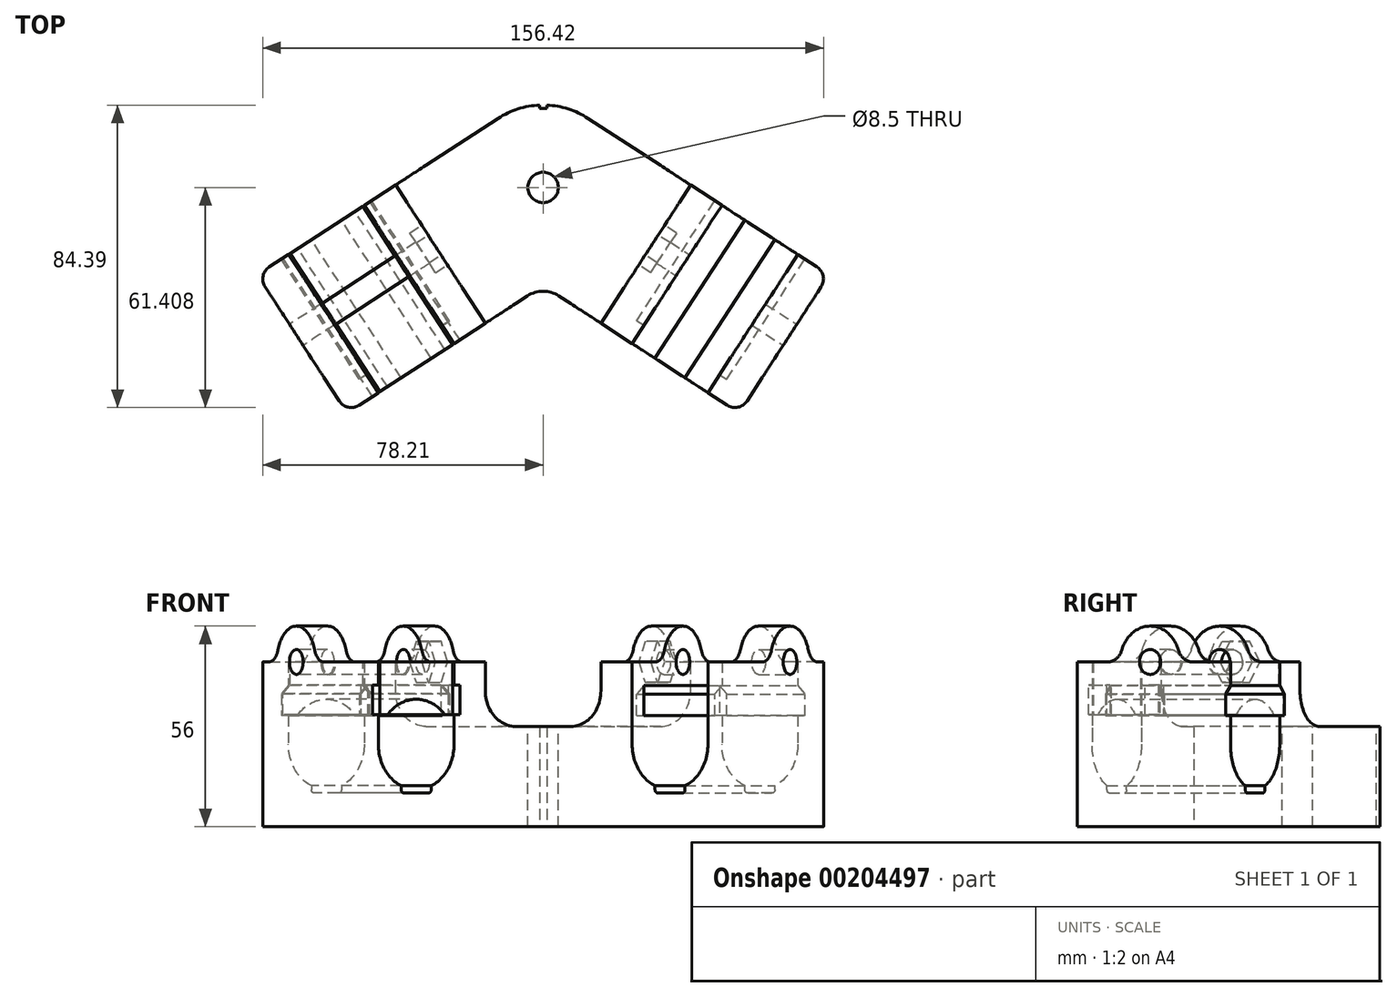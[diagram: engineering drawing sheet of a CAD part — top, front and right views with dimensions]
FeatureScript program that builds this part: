
annotation { "Feature Type Name" : "Feature", "Feature Type Description" : "" }
export const myFeature = defineFeature(function(context is Context, id is Id, definition is map)
    precondition{}
    {
        {
            var Q0;
            Q0=qCreatedBy(makeId("Top.planeOp"),FACE);
            var sketch = newSketch(context, id + "F0", { "sketchPlane" : qUnion([Q0])});
            skCircle(sketch, "E0", {"center": v(0, 0) * mm, "radius": 104.93 * mm, "construction": true});
            skLineSegment(sketch, "E1", {"start": v(0, 0) * mm, "end": v(-57.15, 88) * mm, "construction": true});
            skLineSegment(sketch, "E2", {"start": v(0, 0) * mm, "end": v(57.15, 88) * mm, "construction": true});
            skLineSegment(sketch, "E3", {"start": v(-54.7, 41.99) * mm, "end": v(0, 77.5) * mm});
            skLineSegment(sketch, "E4", {"start": v(-54.7, 41.99) * mm, "end": v(-79.74, 80.57) * mm});
            skLineSegment(sketch, "E5", {"start": v(-79.74, 80.57) * mm, "end": v(-12.53, 124.22) * mm});
            skArc(sketch, "E6", {"start": v(0, 127.93) * mm, "mid": v(-6.53, 126.98) * mm, "end": v(-12.53, 124.22) * mm});
            skLineSegment(sketch, "E7.MirrorCS", {"start": v(54.7, 41.99) * mm, "end": v(0, 77.5) * mm});
            skLineSegment(sketch, "E8.MirrorCS", {"start": v(79.74, 80.57) * mm, "end": v(12.53, 124.22) * mm});
            skLineSegment(sketch, "E9.MirrorCS", {"start": v(54.7, 41.99) * mm, "end": v(79.74, 80.57) * mm});
            skArc(sketch, "E10.MirrorCS", {"start": v(0, 127.93) * mm, "mid": v(6.53, 126.98) * mm, "end": v(12.53, 124.22) * mm});
            skPoint(sketch, "E11", {"position": v(-35.4, 54.51) * mm});
            skPoint(sketch, "E12", {"position": v(35.4, 54.51) * mm});
            skSolve(sketch);
        }
        {
            var Q0;
            Q0 = qSketchRegion(id + "F0", true);
            extrude(context, id + "F1", {"entities" : qUnion([Q0]), "endBound" : BoundingType.SYMMETRIC, "depth" : 46 * mm});
        }
        {
            var Q0;
            Q0=qCreatedBy(makeId("Top.planeOp"),FACE);
            var sketch = newSketch(context, id + "F2", { "sketchPlane" : qUnion([Q0])});
            skLineSegment(sketch, "E13", {"start": v(-45.97, 47.65) * mm, "end": v(-71.02, 86.23) * mm});
            skLineSegment(sketch, "E14", {"start": v(-71.02, 86.23) * mm, "end": v(-60.45, 93.1) * mm});
            skLineSegment(sketch, "E15", {"start": v(-60.45, 93.1) * mm, "end": v(-35.4, 54.51) * mm});
            skLineSegment(sketch, "E16", {"start": v(-35.4, 54.51) * mm, "end": v(-45.97, 47.65) * mm});
            skSolve(sketch);
        }
        {
            var Q0;
            Q0=qCreatedBy(makeId("Top.planeOp"),FACE);
            var sketch = newSketch(context, id + "F3", { "sketchPlane" : qUnion([Q0])});
            skLineSegment(sketch, "E17", {"start": v(24.83, 61.38) * mm, "end": v(49.89, 99.95) * mm});
            skLineSegment(sketch, "E18", {"start": v(49.89, 99.95) * mm, "end": v(60.45, 93.1) * mm});
            skLineSegment(sketch, "E19", {"start": v(60.45, 93.1) * mm, "end": v(35.4, 54.51) * mm});
            skLineSegment(sketch, "E20", {"start": v(35.4, 54.51) * mm, "end": v(24.83, 61.38) * mm});
            skSolve(sketch);
        }
        {
            var Q0;
            Q0 = qSketchRegion(id + "F2", true);
            var Q1;
            Q1=sQuery(id+"F0.wireOp",EDGE,"E1");
            revolve(context, id + "F4", {"operationType" : NewBodyOperationType.REMOVE, "entities" : qUnion([Q0]), "axis" : qUnion([Q1]), "revolveType" : RevolveType.FULL, "oppositeDirection" : true});
        }
        {
            var Q0;
            Q0 = qSketchRegion(id + "F3", true);
            var Q1;
            Q1=sQuery(id+"F0.wireOp",EDGE,"E2");
            revolve(context, id + "F5", {"operationType" : NewBodyOperationType.REMOVE, "entities" : qUnion([Q0]), "axis" : qUnion([Q1]), "revolveType" : RevolveType.FULL, "oppositeDirection" : true});
        }
        {
            var Q0;
            {var subQ0=sQuery(id+"F0.wireOp",EDGE,"E7.MirrorCS");var subQ1=makeQuery(id+"F1.opExtrude","SWEPT_FACE",FACE,{"disambiguationData":[OSD([subQ0])]});var subQ2=sQuery(id+"F0.wireOp",EDGE,"E10.MirrorCS");var subQ3=sQuery(id+"F0.wireOp",EDGE,"E6");var subQ5=sQuery(id+"F0.wireOp",EDGE,"E5");var subQ7=sQuery(id+"F0.wireOp",EDGE,"E3");var subQ8=makeQuery(id+"F1.opExtrude","SWEPT_FACE",FACE,{"disambiguationData":[OSD([subQ7])]});var subQ10=sQuery(id+"F0.wireOp",EDGE,"E8.MirrorCS");var subQ12=sQuery(id+"F0.wireOp",EDGE,"E9.MirrorCS");Q0=makeQuery(id+"F15.boolean.opBoolean","SPLIT",FACE,{"disambiguationData":[TD([subQ8])],"derivedFrom":makeQuery(id+"F14.boolean.opBoolean","SPLIT",FACE,{"disambiguationData":[TD([subQ1])],"derivedFrom":makeQuery(id+"F1.opExtrude","CAP_FACE",FACE,{"disambiguationData":[OSD([subQ7,sQuery(id+"F0.wireOp",EDGE,"E4"),subQ5,subQ3,subQ0,subQ10,subQ12,subQ2])],"isStart":false})})});}
            var sketch = newSketch(context, id + "F6", { "sketchPlane" : qUnion([Q0])});
            skLineSegment(sketch, "E21.0", {"start": v(-41.17, 105.62) * mm, "end": v(-12.53, 124.22) * mm});
            skArc(sketch, "E22.0", {"start": v(0, 127.93) * mm, "mid": v(-6.53, 126.98) * mm, "end": v(-12.53, 124.22) * mm});
            skArc(sketch, "E23.0", {"start": v(0, 127.93) * mm, "mid": v(6.53, 126.98) * mm, "end": v(12.53, 124.22) * mm});
            skLineSegment(sketch, "E24.0", {"start": v(41.17, 105.62) * mm, "end": v(12.53, 124.22) * mm});
            skLineSegment(sketch, "E25.0", {"start": v(16.11, 67.04) * mm, "end": v(0, 77.5) * mm});
            skLineSegment(sketch, "E26.0", {"start": v(-16.11, 67.04) * mm, "end": v(0, 77.5) * mm});
            skLineSegment(sketch, "E27", {"start": v(-41.17, 105.62) * mm, "end": v(-16.11, 67.04) * mm});
            skLineSegment(sketch, "E28", {"start": v(16.11, 67.04) * mm, "end": v(41.17, 105.62) * mm});
            skPoint(sketch, "E29.orphan", {"position": v(-79.74, 80.57) * mm});
            skPoint(sketch, "E30.orphan", {"position": v(-54.7, 41.99) * mm});
            skPoint(sketch, "E31.orphan", {"position": v(54.7, 41.99) * mm});
            skPoint(sketch, "E32.orphan", {"position": v(79.74, 80.57) * mm});
            skSolve(sketch);
        }
        {
            var Q0;
            Q0 = qSketchRegion(id + "F6", true);
            extrude(context, id + "F7", {"entities" : qUnion([Q0]), "operationType" : NewBodyOperationType.REMOVE, "oppositeDirection" : true, "depth" : 18 * mm});
        }
        {
            var Q0;
            Q0=makeQuery(id+"F1.opExtrude","SWEPT_FACE",FACE,{"disambiguationData":[OSD([sQuery(id+"F0.wireOp",EDGE,"E4")])]});
            var sketch = newSketch(context, id + "F8", { "sketchPlane" : qUnion([Q0])});
            skCircle(sketch, "E33", {"center": v(-91, 23) * mm, "radius": 10 * mm});
            skSolve(sketch);
        }
        {
            var Q0;
            Q0=makeQuery(id+"F1.opExtrude","SWEPT_FACE",FACE,{"disambiguationData":[OSD([sQuery(id+"F0.wireOp",EDGE,"E9.MirrorCS")])]});
            var sketch = newSketch(context, id + "F9", { "sketchPlane" : qUnion([Q0])});
            skCircle(sketch, "E34", {"center": v(91, 23) * mm, "radius": 10 * mm});
            skSolve(sketch);
        }
        {
            var Q0;
            Q0 = qSketchRegion(id + "F8", true);
            var Q1;
            Q1=makeQuery(id+"F7.boolean.opBoolean","COPY",FACE,{"derivedFrom":makeQuery(id+"F7.opExtrude","SWEPT_FACE",FACE,{"disambiguationData":[OSD([sQuery(id+"F6.wireOp",EDGE,"E27")])]})});
            extrude(context, id + "F10", {"entities" : qUnion([Q0]), "operationType" : NewBodyOperationType.ADD, "endBound" : BoundingType.UP_TO_SURFACE, "oppositeDirection" : true, "endBoundEntityFace" : qUnion([Q1]), "depth" : 25 * mm});
        }
        {
            var Q0;
            Q0 = qSketchRegion(id + "F9", true);
            var Q1;
            Q1=makeQuery(id+"F7.boolean.opBoolean","COPY",FACE,{"derivedFrom":makeQuery(id+"F7.opExtrude","SWEPT_FACE",FACE,{"disambiguationData":[OSD([sQuery(id+"F6.wireOp",EDGE,"E28")])]})});
            extrude(context, id + "F11", {"entities" : qUnion([Q0]), "operationType" : NewBodyOperationType.ADD, "endBound" : BoundingType.UP_TO_SURFACE, "oppositeDirection" : true, "endBoundEntityFace" : qUnion([Q1]), "depth" : 25 * mm});
        }
        {
            var Q0;
            Q0=qCreatedBy(makeId("Top.planeOp"),FACE);
            var sketch = newSketch(context, id + "F12", { "sketchPlane" : qUnion([Q0])});
            skLineSegment(sketch, "E35.0", {"start": v(-45.97, 47.65) * mm, "end": v(-71.02, 86.23) * mm});
            skLineSegment(sketch, "E36.0", {"start": v(-35.4, 54.51) * mm, "end": v(-45.97, 47.65) * mm});
            skLineSegment(sketch, "E37.0", {"start": v(-71.02, 86.23) * mm, "end": v(-60.45, 93.1) * mm});
            skLineSegment(sketch, "E38.MirrorCS", {"start": v(-35.4, 54.51) * mm, "end": v(-24.83, 61.38) * mm});
            skLineSegment(sketch, "E39.MirrorCS", {"start": v(-24.83, 61.38) * mm, "end": v(-49.89, 99.95) * mm});
            skLineSegment(sketch, "E40.MirrorCS", {"start": v(-49.89, 99.95) * mm, "end": v(-60.45, 93.1) * mm});
            skSolve(sketch);
        }
        {
            var Q0;
            Q0=qCreatedBy(makeId("Top.planeOp"),FACE);
            var sketch = newSketch(context, id + "F13", { "sketchPlane" : qUnion([Q0])});
            skLineSegment(sketch, "E41.0", {"start": v(35.4, 54.51) * mm, "end": v(24.83, 61.38) * mm});
            skLineSegment(sketch, "E42.0", {"start": v(24.83, 61.38) * mm, "end": v(49.89, 99.95) * mm});
            skLineSegment(sketch, "E43.0", {"start": v(49.89, 99.95) * mm, "end": v(60.45, 93.1) * mm});
            skLineSegment(sketch, "E44.MirrorCS", {"start": v(45.97, 47.65) * mm, "end": v(71.02, 86.23) * mm});
            skLineSegment(sketch, "E45.MirrorCS", {"start": v(35.4, 54.51) * mm, "end": v(45.97, 47.65) * mm});
            skLineSegment(sketch, "E46.MirrorCS", {"start": v(71.02, 86.23) * mm, "end": v(60.45, 93.1) * mm});
            skSolve(sketch);
        }
        {
            var Q0;
            Q0 = qSketchRegion(id + "F12", true);
            var Q1;
            Q1=makeQuery(id+"F1.opExtrude","CAP_FACE",FACE,{"disambiguationData":[OSD([sQuery(id+"F0.wireOp",EDGE,"E3"),sQuery(id+"F0.wireOp",EDGE,"E4"),sQuery(id+"F0.wireOp",EDGE,"E5"),sQuery(id+"F0.wireOp",EDGE,"E6"),sQuery(id+"F0.wireOp",EDGE,"E7.MirrorCS"),sQuery(id+"F0.wireOp",EDGE,"E8.MirrorCS"),sQuery(id+"F0.wireOp",EDGE,"E9.MirrorCS"),sQuery(id+"F0.wireOp",EDGE,"E10.MirrorCS")])],"isStart":false});
            extrude(context, id + "F14", {"entities" : qUnion([Q0]), "operationType" : NewBodyOperationType.REMOVE, "endBound" : BoundingType.THROUGH_ALL, "endBoundEntityFace" : qUnion([Q1]), "depth" : 25 * mm});
        }
        {
            var Q0;
            Q0 = qSketchRegion(id + "F13", true);
            var Q1;
            {var subQ0=sQuery(id+"F0.wireOp",EDGE,"E7.MirrorCS");var subQ1=sQuery(id+"F0.wireOp",EDGE,"E8.MirrorCS");var subQ2=sQuery(id+"F0.wireOp",EDGE,"E9.MirrorCS");Q1=makeQuery(id+"F7.boolean.opBoolean","SPLIT",FACE,{"disambiguationData":[TD([makeQuery(id+"F1.opExtrude","SWEPT_FACE",FACE,{"disambiguationData":[OSD([subQ0])]})])],"derivedFrom":makeQuery(id+"F1.opExtrude","CAP_FACE",FACE,{"disambiguationData":[OSD([sQuery(id+"F0.wireOp",EDGE,"E3"),sQuery(id+"F0.wireOp",EDGE,"E4"),sQuery(id+"F0.wireOp",EDGE,"E5"),sQuery(id+"F0.wireOp",EDGE,"E6"),subQ0,subQ1,subQ2,sQuery(id+"F0.wireOp",EDGE,"E10.MirrorCS")])],"isStart":false})});}
            extrude(context, id + "F15", {"entities" : qUnion([Q0]), "operationType" : NewBodyOperationType.REMOVE, "endBound" : BoundingType.THROUGH_ALL, "endBoundEntityFace" : qUnion([Q1]), "depth" : 25 * mm});
        }
        {
            var Q0;
            Q0=makeQuery(id+"F1.opExtrude","SWEPT_EDGE",EDGE,{"disambiguationData":[OSD([sQuery(id+"F0.wireOp",EDGE,"E3"),sQuery(id+"F0.wireOp",EDGE,"E7.MirrorCS")])]});
            fillet(context, id + "F16", {"entities" : qUnion([Q0]), "radius" : 8 * mm, "tangentPropagation" : true, "allowEdgeOverflow" : false});
        }
        {
            var Q0;
            Q0=makeQuery(id+"F7.boolean.opBoolean","COPY",EDGE,{"derivedFrom":makeQuery(id+"F7.opExtrude","CAP_EDGE",EDGE,{"disambiguationData":[OSD([sQuery(id+"F6.wireOp",EDGE,"E28")])],"isStart":false})});
            var Q1;
            Q1=makeQuery(id+"F7.boolean.opBoolean","COPY",EDGE,{"derivedFrom":makeQuery(id+"F7.opExtrude","CAP_EDGE",EDGE,{"disambiguationData":[OSD([sQuery(id+"F6.wireOp",EDGE,"E27")])],"isStart":false})});
            fillet(context, id + "F17", {"entities" : qUnion([Q0, Q1]), "radius" : 10 * mm, "tangentPropagation" : true, "allowEdgeOverflow" : false});
        }
        {
            var Q0;
            Q0=makeQuery(id+"F1.opExtrude","SWEPT_FACE",FACE,{"disambiguationData":[OSD([sQuery(id+"F0.wireOp",EDGE,"E5")])]});
            var sketch = newSketch(context, id + "F18", { "sketchPlane" : qUnion([Q0])});
            skLineSegment(sketch, "E47.bottom", {"start": v(-12.6, 16.4) * mm, "end": v(12.6, 16.4) * mm});
            skLineSegment(sketch, "E47.top", {"start": v(-15, 8) * mm, "end": v(15, 8) * mm});
            skLineSegment(sketch, "E47.left", {"start": v(-15, 14) * mm, "end": v(-15, 8) * mm});
            skLineSegment(sketch, "E47.right", {"start": v(15, 14) * mm, "end": v(15, 8) * mm});
            skLineSegment(sketch, "E48", {"start": v(-12.6, 16.4) * mm, "end": v(-15, 14) * mm});
            skLineSegment(sketch, "E49", {"start": v(12.6, 16.4) * mm, "end": v(15, 14) * mm});
            skSolve(sketch);
        }
        {
            var Q0;
            Q0=makeQuery(id+"F1.opExtrude","SWEPT_FACE",FACE,{"disambiguationData":[OSD([sQuery(id+"F0.wireOp",EDGE,"E8.MirrorCS")])]});
            var sketch = newSketch(context, id + "F19", { "sketchPlane" : qUnion([Q0])});
            skLineSegment(sketch, "E50.bottom", {"start": v(-15, 8) * mm, "end": v(15, 8) * mm});
            skLineSegment(sketch, "E50.top", {"start": v(-12.6, 16.4) * mm, "end": v(12.6, 16.4) * mm});
            skLineSegment(sketch, "E50.left", {"start": v(-15, 8) * mm, "end": v(-15, 14) * mm});
            skLineSegment(sketch, "E50.right", {"start": v(15, 8) * mm, "end": v(15, 14) * mm});
            skLineSegment(sketch, "E51", {"start": v(-12.6, 16.4) * mm, "end": v(-15, 14) * mm});
            skLineSegment(sketch, "E52", {"start": v(12.6, 16.4) * mm, "end": v(15, 14) * mm});
            skSolve(sketch);
        }
        {
            var Q0;
            Q0 = qSketchRegion(id + "F18", true);
            extrude(context, id + "F20", {"entities" : qUnion([Q0]), "operationType" : NewBodyOperationType.REMOVE, "oppositeDirection" : true, "depth" : 40 * mm});
        }
        {
            var Q0;
            Q0 = qSketchRegion(id + "F19", true);
            extrude(context, id + "F21", {"entities" : qUnion([Q0]), "operationType" : NewBodyOperationType.REMOVE, "oppositeDirection" : true, "depth" : 40 * mm});
        }
        {
            var Q0;
            Q0=makeQuery(id+"F1.opExtrude","SWEPT_FACE",FACE,{"disambiguationData":[OSD([sQuery(id+"F0.wireOp",EDGE,"E5")])]});
            var sketch = newSketch(context, id + "F22", { "sketchPlane" : qUnion([Q0])});
            skLineSegment(sketch, "E53.bottom", {"start": v(-5, -10.6) * mm, "end": v(5, -10.6) * mm});
            skLineSegment(sketch, "E53.top", {"start": v(-4, -13.6) * mm, "end": v(4, -13.6) * mm});
            skLineSegment(sketch, "E53.left", {"start": v(-5, -10.6) * mm, "end": v(-5, -12.6) * mm});
            skLineSegment(sketch, "E53.right", {"start": v(5, -10.6) * mm, "end": v(5, -12.6) * mm});
            skLineSegment(sketch, "E54", {"start": v(0, 0) * mm, "end": v(0, -16.56) * mm, "construction": true});
            skPoint(sketch, "E54.endSnap0", {"position": v(0, -12.6) * mm});
            skPoint(sketch, "E55", {"position": v(0, -13.6) * mm});
            skPoint(sketch, "E56.visualSharp", {"position": v(-5, -13.6) * mm});
            skArc(sketch, "E56.filletArc", {"start": v(-5, -12.6) * mm, "mid": v(-4.7, -13.3) * mm, "end": v(-4, -13.6) * mm});
            skPoint(sketch, "E57.visualSharp", {"position": v(5, -13.6) * mm});
            skArc(sketch, "E57.filletArc", {"start": v(4, -13.6) * mm, "mid": v(4.7, -13.3) * mm, "end": v(5, -12.6) * mm});
            skSolve(sketch);
        }
        {
            var Q0;
            Q0=makeQuery(id+"F1.opExtrude","SWEPT_FACE",FACE,{"disambiguationData":[OSD([sQuery(id+"F0.wireOp",EDGE,"E8.MirrorCS")])]});
            var sketch = newSketch(context, id + "F23", { "sketchPlane" : qUnion([Q0])});
            skLineSegment(sketch, "E58.bottom", {"start": v(-4, -13.6) * mm, "end": v(4, -13.6) * mm});
            skLineSegment(sketch, "E58.top", {"start": v(-5, -10.6) * mm, "end": v(5, -10.6) * mm});
            skLineSegment(sketch, "E58.left", {"start": v(-5, -12.6) * mm, "end": v(-5, -10.6) * mm});
            skLineSegment(sketch, "E58.right", {"start": v(5, -12.6) * mm, "end": v(5, -10.6) * mm});
            skLineSegment(sketch, "E59", {"start": v(0, 0) * mm, "end": v(0, -15.9) * mm, "construction": true});
            skPoint(sketch, "E59.endSnap0", {"position": v(0, -12.6) * mm});
            skPoint(sketch, "E60", {"position": v(0, -13.6) * mm});
            skPoint(sketch, "E61.visualSharp", {"position": v(-5, -13.6) * mm});
            skArc(sketch, "E61.filletArc", {"start": v(-5, -12.6) * mm, "mid": v(-4.7, -13.3) * mm, "end": v(-4, -13.6) * mm});
            skPoint(sketch, "E62.visualSharp", {"position": v(5, -13.6) * mm});
            skArc(sketch, "E62.filletArc", {"start": v(4, -13.6) * mm, "mid": v(4.7, -13.3) * mm, "end": v(5, -12.6) * mm});
            skSolve(sketch);
        }
        {
            var Q0;
            Q0 = qSketchRegion(id + "F22", true);
            var Q1;
            Q1=makeQuery(id+"F1.opExtrude","SWEPT_FACE",FACE,{"disambiguationData":[OSD([sQuery(id+"F0.wireOp",EDGE,"E3")])]});
            extrude(context, id + "F24", {"entities" : qUnion([Q0]), "operationType" : NewBodyOperationType.REMOVE, "endBound" : BoundingType.UP_TO_SURFACE, "oppositeDirection" : true, "endBoundEntityFace" : qUnion([Q1]), "depth" : 25 * mm});
        }
        {
            var Q0;
            Q0 = qSketchRegion(id + "F23", true);
            var Q1;
            Q1=makeQuery(id+"F1.opExtrude","SWEPT_FACE",FACE,{"disambiguationData":[OSD([sQuery(id+"F0.wireOp",EDGE,"E7.MirrorCS")])]});
            extrude(context, id + "F25", {"entities" : qUnion([Q0]), "operationType" : NewBodyOperationType.REMOVE, "endBound" : BoundingType.UP_TO_SURFACE, "oppositeDirection" : true, "endBoundEntityFace" : qUnion([Q1]), "depth" : 25 * mm});
        }
        {
            var Q0;
            {var subQ0=sQuery(id+"F9.wireOp",EDGE,"E34");var subQ1=makeQuery(id+"F11.opExtrude","SWEPT_FACE",FACE,{"disambiguationData":[OSD([subQ0])]});var subQ2=sQuery(id+"F0.wireOp",EDGE,"E9.MirrorCS");var subQ3=makeQuery(id+"F1.opExtrude","SWEPT_FACE",FACE,{"disambiguationData":[OSD([subQ2])]});var subQ4=sQuery(id+"F0.wireOp",EDGE,"E8.MirrorCS");var subQ5=sQuery(id+"F0.wireOp",EDGE,"E7.MirrorCS");var subQ6=makeQuery(id+"F1.opExtrude","CAP_FACE",FACE,{"disambiguationData":[OSD([sQuery(id+"F0.wireOp",EDGE,"E3"),sQuery(id+"F0.wireOp",EDGE,"E4"),sQuery(id+"F0.wireOp",EDGE,"E5"),sQuery(id+"F0.wireOp",EDGE,"E6"),subQ5,subQ4,subQ2,sQuery(id+"F0.wireOp",EDGE,"E10.MirrorCS")])],"isStart":false});Q0=makeQuery(id+"F15.boolean.opBoolean","SPLIT",EDGE,{"disambiguationData":[TD([subQ3])],"derivedFrom":makeQuery(id+"F11.boolean.opBoolean","INTERSECT",EDGE,{"disambiguationData":[OD(1.0)],"derivedFrom":[makeQuery(id+"F7.boolean.opBoolean","SPLIT",FACE,{"disambiguationData":[TD([makeQuery(id+"F1.opExtrude","SWEPT_FACE",FACE,{"disambiguationData":[OSD([subQ5])]})])],"derivedFrom":subQ6}),subQ1]})});}
            var Q1;
            {var subQ0=sQuery(id+"F9.wireOp",EDGE,"E34");var subQ1=makeQuery(id+"F11.opExtrude","SWEPT_FACE",FACE,{"disambiguationData":[OSD([subQ0])]});var subQ2=sQuery(id+"F0.wireOp",EDGE,"E9.MirrorCS");var subQ3=makeQuery(id+"F1.opExtrude","SWEPT_FACE",FACE,{"disambiguationData":[OSD([subQ2])]});var subQ4=sQuery(id+"F0.wireOp",EDGE,"E8.MirrorCS");var subQ5=sQuery(id+"F0.wireOp",EDGE,"E7.MirrorCS");var subQ6=makeQuery(id+"F1.opExtrude","CAP_FACE",FACE,{"disambiguationData":[OSD([sQuery(id+"F0.wireOp",EDGE,"E3"),sQuery(id+"F0.wireOp",EDGE,"E4"),sQuery(id+"F0.wireOp",EDGE,"E5"),sQuery(id+"F0.wireOp",EDGE,"E6"),subQ5,subQ4,subQ2,sQuery(id+"F0.wireOp",EDGE,"E10.MirrorCS")])],"isStart":false});Q1=makeQuery(id+"F15.boolean.opBoolean","SPLIT",EDGE,{"disambiguationData":[TD([subQ3])],"derivedFrom":makeQuery(id+"F11.boolean.opBoolean","INTERSECT",EDGE,{"disambiguationData":[OD(0.0)],"derivedFrom":[makeQuery(id+"F7.boolean.opBoolean","SPLIT",FACE,{"disambiguationData":[TD([makeQuery(id+"F1.opExtrude","SWEPT_FACE",FACE,{"disambiguationData":[OSD([subQ5])]})])],"derivedFrom":subQ6}),subQ1]})});}
            var Q2;
            {var subQ0=makeQuery(id+"F11.opExtrude","SWEPT_FACE",FACE,{"disambiguationData":[OSD([sQuery(id+"F9.wireOp",EDGE,"E34")])]});var subQ1=sQuery(id+"F6.wireOp",EDGE,"E28");var subQ2=makeQuery(id+"F7.opExtrude","SWEPT_FACE",FACE,{"disambiguationData":[OSD([subQ1])]});var subQ3=sQuery(id+"F0.wireOp",EDGE,"E9.MirrorCS");var subQ4=sQuery(id+"F0.wireOp",EDGE,"E8.MirrorCS");var subQ5=sQuery(id+"F0.wireOp",EDGE,"E7.MirrorCS");var subQ6=makeQuery(id+"F1.opExtrude","CAP_FACE",FACE,{"disambiguationData":[OSD([sQuery(id+"F0.wireOp",EDGE,"E3"),sQuery(id+"F0.wireOp",EDGE,"E4"),sQuery(id+"F0.wireOp",EDGE,"E5"),sQuery(id+"F0.wireOp",EDGE,"E6"),subQ5,subQ4,subQ3,sQuery(id+"F0.wireOp",EDGE,"E10.MirrorCS")])],"isStart":false});Q2=makeQuery(id+"F15.boolean.opBoolean","SPLIT",EDGE,{"disambiguationData":[TD([makeQuery(id+"F7.boolean.opBoolean","COPY",FACE,{"derivedFrom":subQ2})])],"derivedFrom":makeQuery(id+"F11.boolean.opBoolean","INTERSECT",EDGE,{"disambiguationData":[OD(0.0)],"derivedFrom":[makeQuery(id+"F7.boolean.opBoolean","SPLIT",FACE,{"disambiguationData":[TD([makeQuery(id+"F1.opExtrude","SWEPT_FACE",FACE,{"disambiguationData":[OSD([subQ5])]})])],"derivedFrom":subQ6}),subQ0]})});}
            var Q3;
            {var subQ0=makeQuery(id+"F11.opExtrude","SWEPT_FACE",FACE,{"disambiguationData":[OSD([sQuery(id+"F9.wireOp",EDGE,"E34")])]});var subQ1=sQuery(id+"F6.wireOp",EDGE,"E28");var subQ2=makeQuery(id+"F7.opExtrude","SWEPT_FACE",FACE,{"disambiguationData":[OSD([subQ1])]});var subQ3=sQuery(id+"F0.wireOp",EDGE,"E9.MirrorCS");var subQ4=sQuery(id+"F0.wireOp",EDGE,"E8.MirrorCS");var subQ5=sQuery(id+"F0.wireOp",EDGE,"E7.MirrorCS");var subQ6=makeQuery(id+"F1.opExtrude","CAP_FACE",FACE,{"disambiguationData":[OSD([sQuery(id+"F0.wireOp",EDGE,"E3"),sQuery(id+"F0.wireOp",EDGE,"E4"),sQuery(id+"F0.wireOp",EDGE,"E5"),sQuery(id+"F0.wireOp",EDGE,"E6"),subQ5,subQ4,subQ3,sQuery(id+"F0.wireOp",EDGE,"E10.MirrorCS")])],"isStart":false});Q3=makeQuery(id+"F15.boolean.opBoolean","SPLIT",EDGE,{"disambiguationData":[TD([makeQuery(id+"F7.boolean.opBoolean","COPY",FACE,{"derivedFrom":subQ2})])],"derivedFrom":makeQuery(id+"F11.boolean.opBoolean","INTERSECT",EDGE,{"disambiguationData":[OD(1.0)],"derivedFrom":[makeQuery(id+"F7.boolean.opBoolean","SPLIT",FACE,{"disambiguationData":[TD([makeQuery(id+"F1.opExtrude","SWEPT_FACE",FACE,{"disambiguationData":[OSD([subQ5])]})])],"derivedFrom":subQ6}),subQ0]})});}
            var Q4;
            {var subQ0=makeQuery(id+"F10.opExtrude","SWEPT_FACE",FACE,{"disambiguationData":[OSD([sQuery(id+"F8.wireOp",EDGE,"E33")])]});var subQ1=sQuery(id+"F6.wireOp",EDGE,"E27");var subQ2=makeQuery(id+"F7.opExtrude","SWEPT_FACE",FACE,{"disambiguationData":[OSD([subQ1])]});var subQ3=sQuery(id+"F0.wireOp",EDGE,"E5");var subQ4=sQuery(id+"F0.wireOp",EDGE,"E4");var subQ5=sQuery(id+"F0.wireOp",EDGE,"E3");var subQ6=makeQuery(id+"F1.opExtrude","CAP_FACE",FACE,{"disambiguationData":[OSD([subQ5,subQ4,subQ3,sQuery(id+"F0.wireOp",EDGE,"E6"),sQuery(id+"F0.wireOp",EDGE,"E7.MirrorCS"),sQuery(id+"F0.wireOp",EDGE,"E8.MirrorCS"),sQuery(id+"F0.wireOp",EDGE,"E9.MirrorCS"),sQuery(id+"F0.wireOp",EDGE,"E10.MirrorCS")])],"isStart":false});Q4=makeQuery(id+"F14.boolean.opBoolean","SPLIT",EDGE,{"disambiguationData":[TD([makeQuery(id+"F7.boolean.opBoolean","COPY",FACE,{"derivedFrom":subQ2})])],"derivedFrom":makeQuery(id+"F10.boolean.opBoolean","INTERSECT",EDGE,{"disambiguationData":[OD(1.0)],"derivedFrom":[makeQuery(id+"F7.boolean.opBoolean","SPLIT",FACE,{"disambiguationData":[TD([makeQuery(id+"F1.opExtrude","SWEPT_FACE",FACE,{"disambiguationData":[OSD([subQ5])]})])],"derivedFrom":subQ6}),subQ0]})});}
            var Q5;
            {var subQ0=makeQuery(id+"F10.opExtrude","SWEPT_FACE",FACE,{"disambiguationData":[OSD([sQuery(id+"F8.wireOp",EDGE,"E33")])]});var subQ1=sQuery(id+"F6.wireOp",EDGE,"E27");var subQ2=makeQuery(id+"F7.opExtrude","SWEPT_FACE",FACE,{"disambiguationData":[OSD([subQ1])]});var subQ3=sQuery(id+"F0.wireOp",EDGE,"E5");var subQ4=sQuery(id+"F0.wireOp",EDGE,"E4");var subQ5=sQuery(id+"F0.wireOp",EDGE,"E3");var subQ6=makeQuery(id+"F1.opExtrude","CAP_FACE",FACE,{"disambiguationData":[OSD([subQ5,subQ4,subQ3,sQuery(id+"F0.wireOp",EDGE,"E6"),sQuery(id+"F0.wireOp",EDGE,"E7.MirrorCS"),sQuery(id+"F0.wireOp",EDGE,"E8.MirrorCS"),sQuery(id+"F0.wireOp",EDGE,"E9.MirrorCS"),sQuery(id+"F0.wireOp",EDGE,"E10.MirrorCS")])],"isStart":false});Q5=makeQuery(id+"F14.boolean.opBoolean","SPLIT",EDGE,{"disambiguationData":[TD([makeQuery(id+"F7.boolean.opBoolean","COPY",FACE,{"derivedFrom":subQ2})])],"derivedFrom":makeQuery(id+"F10.boolean.opBoolean","INTERSECT",EDGE,{"disambiguationData":[OD(0.0)],"derivedFrom":[makeQuery(id+"F7.boolean.opBoolean","SPLIT",FACE,{"disambiguationData":[TD([makeQuery(id+"F1.opExtrude","SWEPT_FACE",FACE,{"disambiguationData":[OSD([subQ5])]})])],"derivedFrom":subQ6}),subQ0]})});}
            var Q6;
            {var subQ0=sQuery(id+"F8.wireOp",EDGE,"E33");var subQ1=makeQuery(id+"F10.opExtrude","SWEPT_FACE",FACE,{"disambiguationData":[OSD([subQ0])]});var subQ2=sQuery(id+"F0.wireOp",EDGE,"E4");var subQ3=makeQuery(id+"F1.opExtrude","SWEPT_FACE",FACE,{"disambiguationData":[OSD([subQ2])]});var subQ4=sQuery(id+"F0.wireOp",EDGE,"E5");var subQ5=sQuery(id+"F0.wireOp",EDGE,"E3");var subQ6=makeQuery(id+"F1.opExtrude","CAP_FACE",FACE,{"disambiguationData":[OSD([subQ5,subQ2,subQ4,sQuery(id+"F0.wireOp",EDGE,"E6"),sQuery(id+"F0.wireOp",EDGE,"E7.MirrorCS"),sQuery(id+"F0.wireOp",EDGE,"E8.MirrorCS"),sQuery(id+"F0.wireOp",EDGE,"E9.MirrorCS"),sQuery(id+"F0.wireOp",EDGE,"E10.MirrorCS")])],"isStart":false});Q6=makeQuery(id+"F14.boolean.opBoolean","SPLIT",EDGE,{"disambiguationData":[TD([subQ3])],"derivedFrom":makeQuery(id+"F10.boolean.opBoolean","INTERSECT",EDGE,{"disambiguationData":[OD(0.0)],"derivedFrom":[makeQuery(id+"F7.boolean.opBoolean","SPLIT",FACE,{"disambiguationData":[TD([makeQuery(id+"F1.opExtrude","SWEPT_FACE",FACE,{"disambiguationData":[OSD([subQ5])]})])],"derivedFrom":subQ6}),subQ1]})});}
            var Q7;
            {var subQ0=sQuery(id+"F8.wireOp",EDGE,"E33");var subQ1=makeQuery(id+"F10.opExtrude","SWEPT_FACE",FACE,{"disambiguationData":[OSD([subQ0])]});var subQ2=sQuery(id+"F0.wireOp",EDGE,"E4");var subQ3=makeQuery(id+"F1.opExtrude","SWEPT_FACE",FACE,{"disambiguationData":[OSD([subQ2])]});var subQ4=sQuery(id+"F0.wireOp",EDGE,"E5");var subQ5=sQuery(id+"F0.wireOp",EDGE,"E3");var subQ6=makeQuery(id+"F1.opExtrude","CAP_FACE",FACE,{"disambiguationData":[OSD([subQ5,subQ2,subQ4,sQuery(id+"F0.wireOp",EDGE,"E6"),sQuery(id+"F0.wireOp",EDGE,"E7.MirrorCS"),sQuery(id+"F0.wireOp",EDGE,"E8.MirrorCS"),sQuery(id+"F0.wireOp",EDGE,"E9.MirrorCS"),sQuery(id+"F0.wireOp",EDGE,"E10.MirrorCS")])],"isStart":false});Q7=makeQuery(id+"F14.boolean.opBoolean","SPLIT",EDGE,{"disambiguationData":[TD([subQ3])],"derivedFrom":makeQuery(id+"F10.boolean.opBoolean","INTERSECT",EDGE,{"disambiguationData":[OD(1.0)],"derivedFrom":[makeQuery(id+"F7.boolean.opBoolean","SPLIT",FACE,{"disambiguationData":[TD([makeQuery(id+"F1.opExtrude","SWEPT_FACE",FACE,{"disambiguationData":[OSD([subQ5])]})])],"derivedFrom":subQ6}),subQ1]})});}
            fillet(context, id + "F26", {"entities" : qUnion([Q0, Q1, Q2, Q3, Q4, Q5, Q6, Q7]), "radius" : 5 * mm, "tangentPropagation" : true, "allowEdgeOverflow" : false});
        }
        {
            var Q0;
            Q0=makeQuery(id+"F7.boolean.opBoolean","COPY",FACE,{"derivedFrom":makeQuery(id+"F7.opExtrude","CAP_FACE",FACE,{"disambiguationData":[OSD([sQuery(id+"F6.wireOp",EDGE,"E21.0"),sQuery(id+"F6.wireOp",EDGE,"E22.0"),sQuery(id+"F6.wireOp",EDGE,"E23.0"),sQuery(id+"F6.wireOp",EDGE,"E24.0"),sQuery(id+"F6.wireOp",EDGE,"E25.0"),sQuery(id+"F6.wireOp",EDGE,"E26.0"),sQuery(id+"F6.wireOp",EDGE,"E27"),sQuery(id+"F6.wireOp",EDGE,"E28")])],"isStart":false})});
            var sketch = newSketch(context, id + "F27", { "sketchPlane" : qUnion([Q0])});
            skCircle(sketch, "E63", {"center": v(0, 104.93) * mm, "radius": 4.25 * mm});
            skLineSegment(sketch, "E64", {"start": v(0, 104.93) * mm, "end": v(0, 128.64) * mm, "construction": true});
            skLineSegment(sketch, "E65.bottom", {"start": v(1, 126.93) * mm, "end": v(-1, 126.93) * mm});
            skLineSegment(sketch, "E65.top", {"start": v(1, 128.93) * mm, "end": v(-1, 128.93) * mm});
            skLineSegment(sketch, "E65.left", {"start": v(1, 126.93) * mm, "end": v(1, 128.93) * mm});
            skLineSegment(sketch, "E65.right", {"start": v(-1, 126.93) * mm, "end": v(-1, 128.93) * mm});
            skPoint(sketch, "E66", {"position": v(0, 128.93) * mm});
            skSolve(sketch);
        }
        {
            var Q0;
            Q0 = qSketchRegion(id + "F27", true);
            var Q1;
            Q1=makeQuery(id+"F1.opExtrude","CAP_FACE",FACE,{"disambiguationData":[OSD([sQuery(id+"F0.wireOp",EDGE,"E3"),sQuery(id+"F0.wireOp",EDGE,"E4"),sQuery(id+"F0.wireOp",EDGE,"E5"),sQuery(id+"F0.wireOp",EDGE,"E6"),sQuery(id+"F0.wireOp",EDGE,"E7.MirrorCS"),sQuery(id+"F0.wireOp",EDGE,"E8.MirrorCS"),sQuery(id+"F0.wireOp",EDGE,"E9.MirrorCS"),sQuery(id+"F0.wireOp",EDGE,"E10.MirrorCS")])],"isStart":true});
            extrude(context, id + "F28", {"entities" : qUnion([Q0]), "operationType" : NewBodyOperationType.REMOVE, "endBound" : BoundingType.UP_TO_SURFACE, "oppositeDirection" : true, "endBoundEntityFace" : qUnion([Q1]), "depth" : 25 * mm});
        }
        {
            var Q0;
            Q0=makeQuery(id+"F1.opExtrude","SWEPT_FACE",FACE,{"disambiguationData":[OSD([sQuery(id+"F0.wireOp",EDGE,"E5")])]});
            var sketch = newSketch(context, id + "F29", { "sketchPlane" : qUnion([Q0])});
            skArc(sketch, "E67", {"start": v(0, 12.6) * mm, "mid": v(-5.23, 11.46) * mm, "end": v(-9.52, 8.25) * mm});
            skLineSegment(sketch, "E68", {"start": v(-9.52, 8.25) * mm, "end": v(-14.5, 8.25) * mm});
            skLineSegment(sketch, "E69", {"start": v(-14.5, 8.25) * mm, "end": v(-14.5, 14.15) * mm});
            skLineSegment(sketch, "E70", {"start": v(-12.1, 16.55) * mm, "end": v(-12.1, 23) * mm});
            skLineSegment(sketch, "E71", {"start": v(-12.1, 23) * mm, "end": v(0, 23) * mm});
            skLineSegment(sketch, "E72", {"start": v(0, 0) * mm, "end": v(0, 25.7) * mm, "construction": true});
            skLineSegment(sketch, "E73", {"start": v(-14.5, 14.15) * mm, "end": v(-12.1, 16.55) * mm});
            skLineSegment(sketch, "E74.MirrorCS", {"start": v(14.5, 8.25) * mm, "end": v(14.5, 14.15) * mm});
            skLineSegment(sketch, "E75.MirrorCS", {"start": v(12.1, 16.55) * mm, "end": v(12.1, 23) * mm});
            skLineSegment(sketch, "E76.MirrorCS", {"start": v(9.52, 8.25) * mm, "end": v(14.5, 8.25) * mm});
            skArc(sketch, "E77.MirrorCS", {"start": v(0, 12.6) * mm, "mid": v(5.23, 11.46) * mm, "end": v(9.52, 8.25) * mm});
            skLineSegment(sketch, "E78.MirrorCS", {"start": v(14.5, 14.15) * mm, "end": v(12.1, 16.55) * mm});
            skLineSegment(sketch, "E79.MirrorCS", {"start": v(12.1, 23) * mm, "end": v(0, 23) * mm});
            skSolve(sketch);
        }
        {
            var Q0;
            Q0 = qSketchRegion(id + "F29", true);
            var Q1;
            Q1=makeQuery(id+"F1.opExtrude","SWEPT_FACE",FACE,{"disambiguationData":[OSD([sQuery(id+"F0.wireOp",EDGE,"E3")])]});
            extrude(context, id + "F30", {"entities" : qUnion([Q0]), "endBound" : BoundingType.UP_TO_SURFACE, "oppositeDirection" : true, "endBoundEntityFace" : qUnion([Q1]), "depth" : 39.5 * mm});
        }
        {
            var Q0;
            Q0=makeQuery(id+"F10.boolean.opBoolean","MERGE",FACE,{"derivedFrom":[makeQuery(id+"F1.opExtrude","SWEPT_FACE",FACE,{"disambiguationData":[OSD([sQuery(id+"F0.wireOp",EDGE,"E4")])]}),makeQuery(id+"F10.opExtrude","CAP_FACE",FACE,{"disambiguationData":[OSD([sQuery(id+"F8.wireOp",EDGE,"E33")])],"isStart":true})]});
            var sketch = newSketch(context, id + "F31", { "sketchPlane" : qUnion([Q0])});
            skCircle(sketch, "E80", {"center": v(-91, 23) * mm, "radius": 3.5 * mm});
            skSolve(sketch);
        }
        {
            var Q0;
            Q0 = qSketchRegion(id + "F31", true);
            var Q1;
            {var subQ0=sQuery(id+"F6.wireOp",EDGE,"E27");Q1=makeQuery(id+"F10.boolean.opBoolean","MERGE",FACE,{"derivedFrom":[makeQuery(id+"F7.boolean.opBoolean","COPY",FACE,{"derivedFrom":makeQuery(id+"F7.opExtrude","SWEPT_FACE",FACE,{"disambiguationData":[OSD([subQ0])]})}),makeQuery(id+"F10.opExtrude","CAP_FACE",FACE,{"disambiguationData":[OSD([subQ0])],"isStart":false})]});}
            extrude(context, id + "F32", {"entities" : qUnion([Q0]), "operationType" : NewBodyOperationType.REMOVE, "endBound" : BoundingType.UP_TO_SURFACE, "oppositeDirection" : true, "endBoundEntityFace" : qUnion([Q1]), "depth" : 25 * mm});
        }
        {
            var Q0;
            Q0=makeQuery(id+"F11.boolean.opBoolean","MERGE",FACE,{"derivedFrom":[makeQuery(id+"F1.opExtrude","SWEPT_FACE",FACE,{"disambiguationData":[OSD([sQuery(id+"F0.wireOp",EDGE,"E9.MirrorCS")])]}),makeQuery(id+"F11.opExtrude","CAP_FACE",FACE,{"disambiguationData":[OSD([sQuery(id+"F9.wireOp",EDGE,"E34")])],"isStart":true})]});
            var sketch = newSketch(context, id + "F33", { "sketchPlane" : qUnion([Q0])});
            skCircle(sketch, "E81", {"center": v(91, 23) * mm, "radius": 3.5 * mm});
            skSolve(sketch);
        }
        {
            var Q0;
            Q0 = qSketchRegion(id + "F33", true);
            var Q1;
            {var subQ0=sQuery(id+"F6.wireOp",EDGE,"E28");Q1=makeQuery(id+"F11.boolean.opBoolean","MERGE",FACE,{"derivedFrom":[makeQuery(id+"F7.boolean.opBoolean","COPY",FACE,{"derivedFrom":makeQuery(id+"F7.opExtrude","SWEPT_FACE",FACE,{"disambiguationData":[OSD([subQ0])]})}),makeQuery(id+"F11.opExtrude","CAP_FACE",FACE,{"disambiguationData":[OSD([subQ0])],"isStart":false})]});}
            extrude(context, id + "F34", {"entities" : qUnion([Q0]), "operationType" : NewBodyOperationType.REMOVE, "endBound" : BoundingType.UP_TO_SURFACE, "oppositeDirection" : true, "endBoundEntityFace" : qUnion([Q1]), "depth" : 25 * mm});
        }
        {
            var Q0;
            {var subQ0=sQuery(id+"F6.wireOp",EDGE,"E27");Q0=makeQuery(id+"F10.boolean.opBoolean","MERGE",FACE,{"derivedFrom":[makeQuery(id+"F7.boolean.opBoolean","COPY",FACE,{"derivedFrom":makeQuery(id+"F7.opExtrude","SWEPT_FACE",FACE,{"disambiguationData":[OSD([subQ0])]})}),makeQuery(id+"F10.opExtrude","CAP_FACE",FACE,{"disambiguationData":[OSD([subQ0])],"isStart":false})]});}
            var sketch = newSketch(context, id + "F35", { "sketchPlane" : qUnion([Q0])});
            skCircle(sketch, "E82.cCircle", {"center": v(91, 23) * mm, "radius": 5.75 * mm, "construction": true});
            skLineSegment(sketch, "E82.0", {"start": v(84.36, 23) * mm, "end": v(87.68, 28.75) * mm});
            skLineSegment(sketch, "E82.1", {"start": v(87.68, 28.75) * mm, "end": v(94.32, 28.75) * mm});
            skLineSegment(sketch, "E82.2", {"start": v(94.32, 28.75) * mm, "end": v(97.64, 23) * mm});
            skLineSegment(sketch, "E82.3", {"start": v(97.64, 23) * mm, "end": v(94.32, 17.25) * mm});
            skLineSegment(sketch, "E82.4", {"start": v(94.32, 17.25) * mm, "end": v(87.68, 17.25) * mm});
            skLineSegment(sketch, "E82.5", {"start": v(87.68, 17.25) * mm, "end": v(84.36, 23) * mm});
            skPoint(sketch, "E82.0.midPoint", {"position": v(86.02, 25.88) * mm});
            skSolve(sketch);
        }
        {
            var Q0;
            Q0 = qSketchRegion(id + "F35", true);
            extrude(context, id + "F36", {"entities" : qUnion([Q0]), "operationType" : NewBodyOperationType.REMOVE, "oppositeDirection" : true, "depth" : 4 * mm});
        }
        {
            var Q0;
            {var subQ0=sQuery(id+"F6.wireOp",EDGE,"E28");Q0=makeQuery(id+"F11.boolean.opBoolean","MERGE",FACE,{"derivedFrom":[makeQuery(id+"F7.boolean.opBoolean","COPY",FACE,{"derivedFrom":makeQuery(id+"F7.opExtrude","SWEPT_FACE",FACE,{"disambiguationData":[OSD([subQ0])]})}),makeQuery(id+"F11.opExtrude","CAP_FACE",FACE,{"disambiguationData":[OSD([subQ0])],"isStart":false})]});}
            var sketch = newSketch(context, id + "F37", { "sketchPlane" : qUnion([Q0])});
            skCircle(sketch, "E83.cCircle", {"center": v(-91, 23) * mm, "radius": 5.75 * mm, "construction": true});
            skLineSegment(sketch, "E83.0", {"start": v(-97.64, 23) * mm, "end": v(-94.32, 28.75) * mm});
            skLineSegment(sketch, "E83.1", {"start": v(-94.32, 28.75) * mm, "end": v(-87.68, 28.75) * mm});
            skLineSegment(sketch, "E83.2", {"start": v(-87.68, 28.75) * mm, "end": v(-84.36, 23) * mm});
            skLineSegment(sketch, "E83.3", {"start": v(-84.36, 23) * mm, "end": v(-87.68, 17.25) * mm});
            skLineSegment(sketch, "E83.4", {"start": v(-87.68, 17.25) * mm, "end": v(-94.32, 17.25) * mm});
            skLineSegment(sketch, "E83.5", {"start": v(-94.32, 17.25) * mm, "end": v(-97.64, 23) * mm});
            skPoint(sketch, "E83.0.midPoint", {"position": v(-95.98, 25.88) * mm});
            skSolve(sketch);
        }
        {
            var Q0;
            Q0 = qSketchRegion(id + "F37", true);
            extrude(context, id + "F38", {"entities" : qUnion([Q0]), "operationType" : NewBodyOperationType.REMOVE, "oppositeDirection" : true, "depth" : 4 * mm});
        }
        {
            var Q0;
            Q0=makeQuery(id+"F1.opExtrude","SWEPT_EDGE",EDGE,{"disambiguationData":[OSD([sQuery(id+"F0.wireOp",EDGE,"E8.MirrorCS"),sQuery(id+"F0.wireOp",EDGE,"E9.MirrorCS")])]});
            var Q1;
            Q1=makeQuery(id+"F1.opExtrude","SWEPT_EDGE",EDGE,{"disambiguationData":[OSD([sQuery(id+"F0.wireOp",EDGE,"E7.MirrorCS"),sQuery(id+"F0.wireOp",EDGE,"E9.MirrorCS")])]});
            var Q2;
            Q2=makeQuery(id+"F1.opExtrude","SWEPT_EDGE",EDGE,{"disambiguationData":[OSD([sQuery(id+"F0.wireOp",EDGE,"E3"),sQuery(id+"F0.wireOp",EDGE,"E4")])]});
            var Q3;
            Q3=makeQuery(id+"F1.opExtrude","SWEPT_EDGE",EDGE,{"disambiguationData":[OSD([sQuery(id+"F0.wireOp",EDGE,"E4"),sQuery(id+"F0.wireOp",EDGE,"E5")])]});
            fillet(context, id + "F39", {"entities" : qUnion([Q0, Q1, Q2, Q3]), "radius" : 4 * mm, "tangentPropagation" : true, "allowEdgeOverflow" : false});
        }
        {
            var Q0;
            Q0=makeQuery(id+"F30.opExtrude","SWEPT_FACE",FACE,{"disambiguationData":[OSD([sQuery(id+"F29.wireOp",EDGE,"E74.MirrorCS")])]});
            var sketch = newSketch(context, id + "F40", { "sketchPlane" : qUnion([Q0])});
            skLineSegment(sketch, "E84", {"start": v(-71, 16.55) * mm, "end": v(-71, 8.25) * mm});
            skLineSegment(sketch, "E85", {"start": v(-71, 8.25) * mm, "end": v(-65, 8.25) * mm});
            skLineSegment(sketch, "E86", {"start": v(-65, 8.25) * mm, "end": v(-65, 16.55) * mm});
            skLineSegment(sketch, "E87", {"start": v(-65, 16.55) * mm, "end": v(-71, 16.55) * mm});
            skSolve(sketch);
        }
        {
            var Q0;
            Q0 = qSketchRegion(id + "F40", true);
            var Q1;
            Q1=makeQuery(id+"F30.opExtrude","SWEPT_FACE",FACE,{"disambiguationData":[OSD([sQuery(id+"F29.wireOp",EDGE,"E75.MirrorCS")])]});
            extrude(context, id + "F41", {"entities" : qUnion([Q0]), "operationType" : NewBodyOperationType.REMOVE, "endBound" : BoundingType.UP_TO_SURFACE, "oppositeDirection" : true, "endBoundEntityFace" : qUnion([Q1]), "depth" : 25 * mm});
        }
        {
            var Q0;
            Q0=makeQuery(id+"F30.opExtrude","SWEPT_FACE",FACE,{"disambiguationData":[OSD([sQuery(id+"F29.wireOp",EDGE,"E69")])]});
            var sketch = newSketch(context, id + "F42", { "sketchPlane" : qUnion([Q0])});
            skLineSegment(sketch, "E88.0", {"start": v(65, 16.55) * mm, "end": v(71, 16.55) * mm});
            skLineSegment(sketch, "E89.0", {"start": v(71, 16.55) * mm, "end": v(71, 8.25) * mm});
            skLineSegment(sketch, "E90.0", {"start": v(71, 8.25) * mm, "end": v(65, 8.25) * mm});
            skLineSegment(sketch, "E91.0", {"start": v(65, 8.25) * mm, "end": v(65, 16.55) * mm});
            skSolve(sketch);
        }
        {
            var Q0;
            Q0 = qSketchRegion(id + "F42", true);
            var Q1;
            Q1=makeQuery(id+"F30.opExtrude","SWEPT_FACE",FACE,{"disambiguationData":[OSD([sQuery(id+"F29.wireOp",EDGE,"E70")])]});
            extrude(context, id + "F43", {"entities" : qUnion([Q0]), "operationType" : NewBodyOperationType.REMOVE, "endBound" : BoundingType.UP_TO_SURFACE, "oppositeDirection" : true, "endBoundEntityFace" : qUnion([Q1]), "depth" : 25 * mm});
        }
    });
